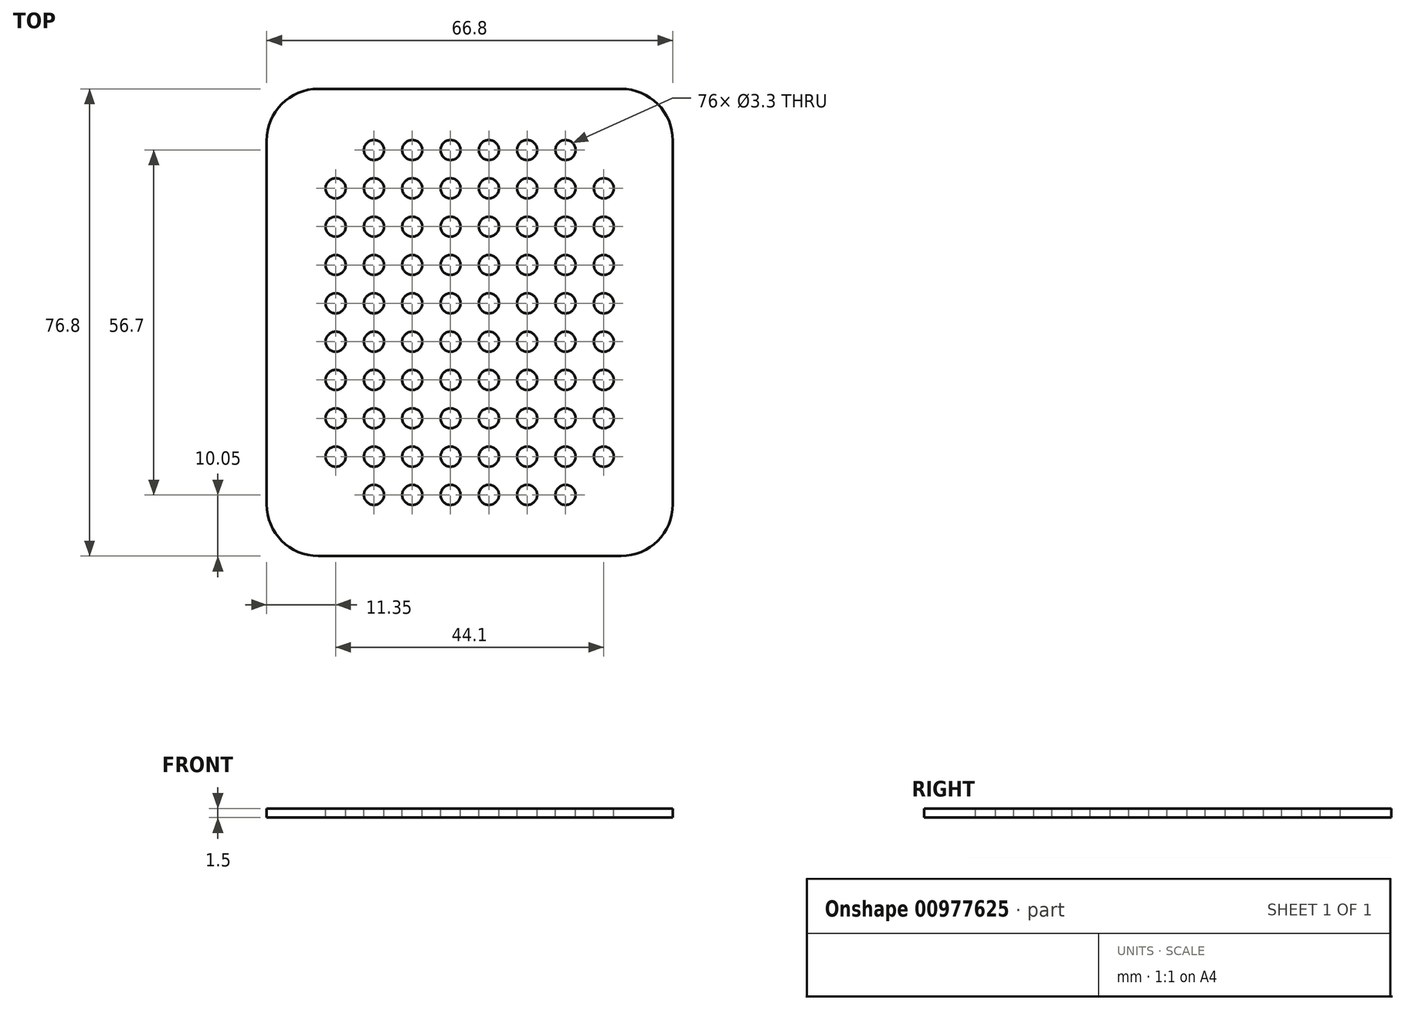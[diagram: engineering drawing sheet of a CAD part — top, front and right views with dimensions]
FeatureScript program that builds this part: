
annotation { "Feature Type Name" : "Feature", "Feature Type Description" : "" }
export const myFeature = defineFeature(function(context is Context, id is Id, definition is map)
    precondition{}
    {
        {
            var Q0;
            Q0=qCreatedBy(makeId("Top.planeOp"),FACE);
            var sketch = newSketch(context, id + "F0", { "sketchPlane" : qUnion([Q0])});
            skLineSegment(sketch, "E0.bottom", {"start": v(24.9, 38.4) * mm, "end": v(-24.9, 38.4) * mm});
            skLineSegment(sketch, "E0.top", {"start": v(24.9, -38.4) * mm, "end": v(-24.9, -38.4) * mm});
            skLineSegment(sketch, "E0.left", {"start": v(33.4, 29.9) * mm, "end": v(33.4, -29.9) * mm});
            skLineSegment(sketch, "E0.right", {"start": v(-33.4, 29.9) * mm, "end": v(-33.4, -29.9) * mm});
            skPoint(sketch, "E0.middle", {"position": v(0, 0) * mm});
            skPoint(sketch, "E1.visualSharp", {"position": v(-33.4, 38.4) * mm});
            skArc(sketch, "E1.filletArc", {"start": v(-24.9, 38.4) * mm, "mid": v(-30.91, 35.91) * mm, "end": v(-33.4, 29.9) * mm});
            skPoint(sketch, "E2.visualSharp", {"position": v(33.4, 38.4) * mm});
            skArc(sketch, "E2.filletArc", {"start": v(33.4, 29.9) * mm, "mid": v(30.91, 35.91) * mm, "end": v(24.9, 38.4) * mm});
            skPoint(sketch, "E3.visualSharp", {"position": v(33.4, -38.4) * mm});
            skArc(sketch, "E3.filletArc", {"start": v(24.9, -38.4) * mm, "mid": v(30.91, -35.91) * mm, "end": v(33.4, -29.9) * mm});
            skPoint(sketch, "E4.visualSharp", {"position": v(-33.4, -38.4) * mm});
            skArc(sketch, "E4.filletArc", {"start": v(-33.4, -29.9) * mm, "mid": v(-30.91, -35.91) * mm, "end": v(-24.9, -38.4) * mm});
            skSolve(sketch);
        }
        {
            var Q0;
            Q0=makeQuery(id+"F0.imprint","IMPRINT",FACE,{"disambiguationData":[TD([[makeQuery(id+"F0.imprint","IMPRINT",EDGE,{"derivedFrom":sQuery(id+"F0.wireOp",EDGE,"E0.bottom")}),1.0]])]});
            extrude(context, id + "F1", {"entities" : qUnion([Q0]), "depth" : 1.5 * mm, "offsetDistance" : 25 * mm});
        }
        {
            var Q0;
            Q0=makeQuery(id+"F1.opExtrude","CAP_FACE",FACE,{"disambiguationData":[OSD([sQuery(id+"F0.wireOp",EDGE,"E0.bottom"),sQuery(id+"F0.wireOp",EDGE,"E0.top"),sQuery(id+"F0.wireOp",EDGE,"E0.left"),sQuery(id+"F0.wireOp",EDGE,"E0.right"),sQuery(id+"F0.wireOp",EDGE,"E1.filletArc"),sQuery(id+"F0.wireOp",EDGE,"E2.filletArc"),sQuery(id+"F0.wireOp",EDGE,"E3.filletArc"),sQuery(id+"F0.wireOp",EDGE,"E4.filletArc")])],"isStart":false});
            var sketch = newSketch(context, id + "F2", { "sketchPlane" : qUnion([Q0])});
            skSolve(sketch);
        }
        {
            var Q0;
            {var subQ3=sQuery(id+"F0.wireOp",EDGE,"E0.bottom");Q0=makeQuery(id+"F2.imprint","IMPRINT",FACE,{"disambiguationData":[TD([[makeQuery(id+"F2.imprint","IMPRINT",EDGE,{"derivedFrom":makeQuery(id+"F1.opExtrude","CAP_EDGE",EDGE,{"disambiguationData":[OSD([subQ3])],"isStart":false})}),1.0]])]});}
            var sketch = newSketch(context, id + "F3", { "sketchPlane" : qUnion([Q0])});
            skCircle(sketch, "E5.1.1.0", {"center": v(-22.05, 22.05) * mm, "radius": 1.65 * mm});
            skCircle(sketch, "E5.1.2.0", {"center": v(-22.05, 15.75) * mm, "radius": 1.65 * mm});
            skCircle(sketch, "E5.1.3.0", {"center": v(-22.05, 9.45) * mm, "radius": 1.65 * mm});
            skCircle(sketch, "E5.1.4.0", {"center": v(-22.05, 3.15) * mm, "radius": 1.65 * mm});
            skCircle(sketch, "E5.1.5.0", {"center": v(-22.05, -3.15) * mm, "radius": 1.65 * mm});
            skCircle(sketch, "E5.1.6.0", {"center": v(-22.05, -9.45) * mm, "radius": 1.65 * mm});
            skCircle(sketch, "E5.1.7.0", {"center": v(-22.05, -15.75) * mm, "radius": 1.65 * mm});
            skCircle(sketch, "E5.1.8.0", {"center": v(-22.05, -22.05) * mm, "radius": 1.65 * mm});
            skCircle(sketch, "E5.2.0.0", {"center": v(-15.75, 28.35) * mm, "radius": 1.65 * mm});
            skCircle(sketch, "E5.2.1.0", {"center": v(-15.75, 22.05) * mm, "radius": 1.65 * mm});
            skCircle(sketch, "E5.2.2.0", {"center": v(-15.75, 15.75) * mm, "radius": 1.65 * mm});
            skCircle(sketch, "E5.2.3.0", {"center": v(-15.75, 9.45) * mm, "radius": 1.65 * mm});
            skCircle(sketch, "E5.2.4.0", {"center": v(-15.75, 3.15) * mm, "radius": 1.65 * mm});
            skCircle(sketch, "E5.2.5.0", {"center": v(-15.75, -3.15) * mm, "radius": 1.65 * mm});
            skCircle(sketch, "E5.2.6.0", {"center": v(-15.75, -9.45) * mm, "radius": 1.65 * mm});
            skCircle(sketch, "E5.2.7.0", {"center": v(-15.75, -15.75) * mm, "radius": 1.65 * mm});
            skCircle(sketch, "E5.2.8.0", {"center": v(-15.75, -22.05) * mm, "radius": 1.65 * mm});
            skCircle(sketch, "E5.2.9.0", {"center": v(-15.75, -28.35) * mm, "radius": 1.65 * mm});
            skCircle(sketch, "E5.3.0.0", {"center": v(-9.45, 28.35) * mm, "radius": 1.65 * mm});
            skCircle(sketch, "E5.3.1.0", {"center": v(-9.45, 22.05) * mm, "radius": 1.65 * mm});
            skCircle(sketch, "E5.3.2.0", {"center": v(-9.45, 15.75) * mm, "radius": 1.65 * mm});
            skCircle(sketch, "E5.3.3.0", {"center": v(-9.45, 9.45) * mm, "radius": 1.65 * mm});
            skCircle(sketch, "E5.3.4.0", {"center": v(-9.45, 3.15) * mm, "radius": 1.65 * mm});
            skCircle(sketch, "E5.3.5.0", {"center": v(-9.45, -3.15) * mm, "radius": 1.65 * mm});
            skCircle(sketch, "E5.3.6.0", {"center": v(-9.45, -9.45) * mm, "radius": 1.65 * mm});
            skCircle(sketch, "E5.3.7.0", {"center": v(-9.45, -15.75) * mm, "radius": 1.65 * mm});
            skCircle(sketch, "E5.3.8.0", {"center": v(-9.45, -22.05) * mm, "radius": 1.65 * mm});
            skCircle(sketch, "E5.3.9.0", {"center": v(-9.45, -28.35) * mm, "radius": 1.65 * mm});
            skCircle(sketch, "E5.4.0.0", {"center": v(-3.15, 28.35) * mm, "radius": 1.65 * mm});
            skCircle(sketch, "E5.4.1.0", {"center": v(-3.15, 22.05) * mm, "radius": 1.65 * mm});
            skCircle(sketch, "E5.4.2.0", {"center": v(-3.15, 15.75) * mm, "radius": 1.65 * mm});
            skCircle(sketch, "E5.4.3.0", {"center": v(-3.15, 9.45) * mm, "radius": 1.65 * mm});
            skCircle(sketch, "E5.4.4.0", {"center": v(-3.15, 3.15) * mm, "radius": 1.65 * mm});
            skCircle(sketch, "E5.4.5.0", {"center": v(-3.15, -3.15) * mm, "radius": 1.65 * mm});
            skCircle(sketch, "E5.4.6.0", {"center": v(-3.15, -9.45) * mm, "radius": 1.65 * mm});
            skCircle(sketch, "E5.4.7.0", {"center": v(-3.15, -15.75) * mm, "radius": 1.65 * mm});
            skCircle(sketch, "E5.4.8.0", {"center": v(-3.15, -22.05) * mm, "radius": 1.65 * mm});
            skCircle(sketch, "E5.4.9.0", {"center": v(-3.15, -28.35) * mm, "radius": 1.65 * mm});
            skCircle(sketch, "E5.5.0.0", {"center": v(3.15, 28.35) * mm, "radius": 1.65 * mm});
            skCircle(sketch, "E5.5.1.0", {"center": v(3.15, 22.05) * mm, "radius": 1.65 * mm});
            skCircle(sketch, "E5.5.2.0", {"center": v(3.15, 15.75) * mm, "radius": 1.65 * mm});
            skCircle(sketch, "E5.5.3.0", {"center": v(3.15, 9.45) * mm, "radius": 1.65 * mm});
            skCircle(sketch, "E5.5.4.0", {"center": v(3.15, 3.15) * mm, "radius": 1.65 * mm});
            skCircle(sketch, "E5.5.5.0", {"center": v(3.15, -3.15) * mm, "radius": 1.65 * mm});
            skCircle(sketch, "E5.5.6.0", {"center": v(3.15, -9.45) * mm, "radius": 1.65 * mm});
            skCircle(sketch, "E5.5.7.0", {"center": v(3.15, -15.75) * mm, "radius": 1.65 * mm});
            skCircle(sketch, "E5.5.8.0", {"center": v(3.15, -22.05) * mm, "radius": 1.65 * mm});
            skCircle(sketch, "E5.5.9.0", {"center": v(3.15, -28.35) * mm, "radius": 1.65 * mm});
            skCircle(sketch, "E5.6.0.0", {"center": v(9.45, 28.35) * mm, "radius": 1.65 * mm});
            skCircle(sketch, "E5.6.1.0", {"center": v(9.45, 22.05) * mm, "radius": 1.65 * mm});
            skCircle(sketch, "E5.6.2.0", {"center": v(9.45, 15.75) * mm, "radius": 1.65 * mm});
            skCircle(sketch, "E5.6.3.0", {"center": v(9.45, 9.45) * mm, "radius": 1.65 * mm});
            skCircle(sketch, "E5.6.4.0", {"center": v(9.45, 3.15) * mm, "radius": 1.65 * mm});
            skCircle(sketch, "E5.6.5.0", {"center": v(9.45, -3.15) * mm, "radius": 1.65 * mm});
            skCircle(sketch, "E5.6.6.0", {"center": v(9.45, -9.45) * mm, "radius": 1.65 * mm});
            skCircle(sketch, "E5.6.7.0", {"center": v(9.45, -15.75) * mm, "radius": 1.65 * mm});
            skCircle(sketch, "E5.6.8.0", {"center": v(9.45, -22.05) * mm, "radius": 1.65 * mm});
            skCircle(sketch, "E5.6.9.0", {"center": v(9.45, -28.35) * mm, "radius": 1.65 * mm});
            skCircle(sketch, "E5.7.0.0", {"center": v(15.75, 28.35) * mm, "radius": 1.65 * mm});
            skCircle(sketch, "E5.7.1.0", {"center": v(15.75, 22.05) * mm, "radius": 1.65 * mm});
            skCircle(sketch, "E5.7.2.0", {"center": v(15.75, 15.75) * mm, "radius": 1.65 * mm});
            skCircle(sketch, "E5.7.3.0", {"center": v(15.75, 9.45) * mm, "radius": 1.65 * mm});
            skCircle(sketch, "E5.7.4.0", {"center": v(15.75, 3.15) * mm, "radius": 1.65 * mm});
            skCircle(sketch, "E5.7.5.0", {"center": v(15.75, -3.15) * mm, "radius": 1.65 * mm});
            skCircle(sketch, "E5.7.6.0", {"center": v(15.75, -9.45) * mm, "radius": 1.65 * mm});
            skCircle(sketch, "E5.7.7.0", {"center": v(15.75, -15.75) * mm, "radius": 1.65 * mm});
            skCircle(sketch, "E5.7.8.0", {"center": v(15.75, -22.05) * mm, "radius": 1.65 * mm});
            skCircle(sketch, "E5.7.9.0", {"center": v(15.75, -28.35) * mm, "radius": 1.65 * mm});
            skCircle(sketch, "E5.8.1.0", {"center": v(22.05, 22.05) * mm, "radius": 1.65 * mm});
            skCircle(sketch, "E5.8.2.0", {"center": v(22.05, 15.75) * mm, "radius": 1.65 * mm});
            skCircle(sketch, "E5.8.3.0", {"center": v(22.05, 9.45) * mm, "radius": 1.65 * mm});
            skCircle(sketch, "E5.8.4.0", {"center": v(22.05, 3.15) * mm, "radius": 1.65 * mm});
            skCircle(sketch, "E5.8.5.0", {"center": v(22.05, -3.15) * mm, "radius": 1.65 * mm});
            skCircle(sketch, "E5.8.6.0", {"center": v(22.05, -9.45) * mm, "radius": 1.65 * mm});
            skCircle(sketch, "E5.8.7.0", {"center": v(22.05, -15.75) * mm, "radius": 1.65 * mm});
            skCircle(sketch, "E5.8.8.0", {"center": v(22.05, -22.05) * mm, "radius": 1.65 * mm});
            skSolve(sketch);
        }
        {
            var Q0;
            Q0 = qSketchRegion(id + "F3", true);
            extrude(context, id + "F4", {"entities" : qUnion([Q0]), "operationType" : NewBodyOperationType.REMOVE, "oppositeDirection" : true, "depth" : 12.2 * mm, "offsetDistance" : 25 * mm, "hasSecondDirection" : true, "secondDirectionOppositeDirection" : false, "secondDirectionDepth" : 25 * mm});
        }
    });
